AUTODESK INVENTOR PART (.ipt)
format: ipt  version: 2020 (Build 240168000, 168)  size: 79,360 bytes
history: native  units: mm
features: sketch x2, sweep x1
ambient origin geometry x8: Origin, YZ Plane, XZ Plane, XY Plane, X Axis, Y Axis, Z Axis, Center Point
bodies: Volumenkörper1 (feature_tree)
feature tree (3):
  sweep  "Sweeping1"
  sketch  "Skizze1"  dims[d0=0.5mm d1=2.0mm]
  sketch  "Skizze2"  dims[d2=4.0mm d3=14.0mm d4=2.0mm d5=0.0mm d6=0.0mm]
